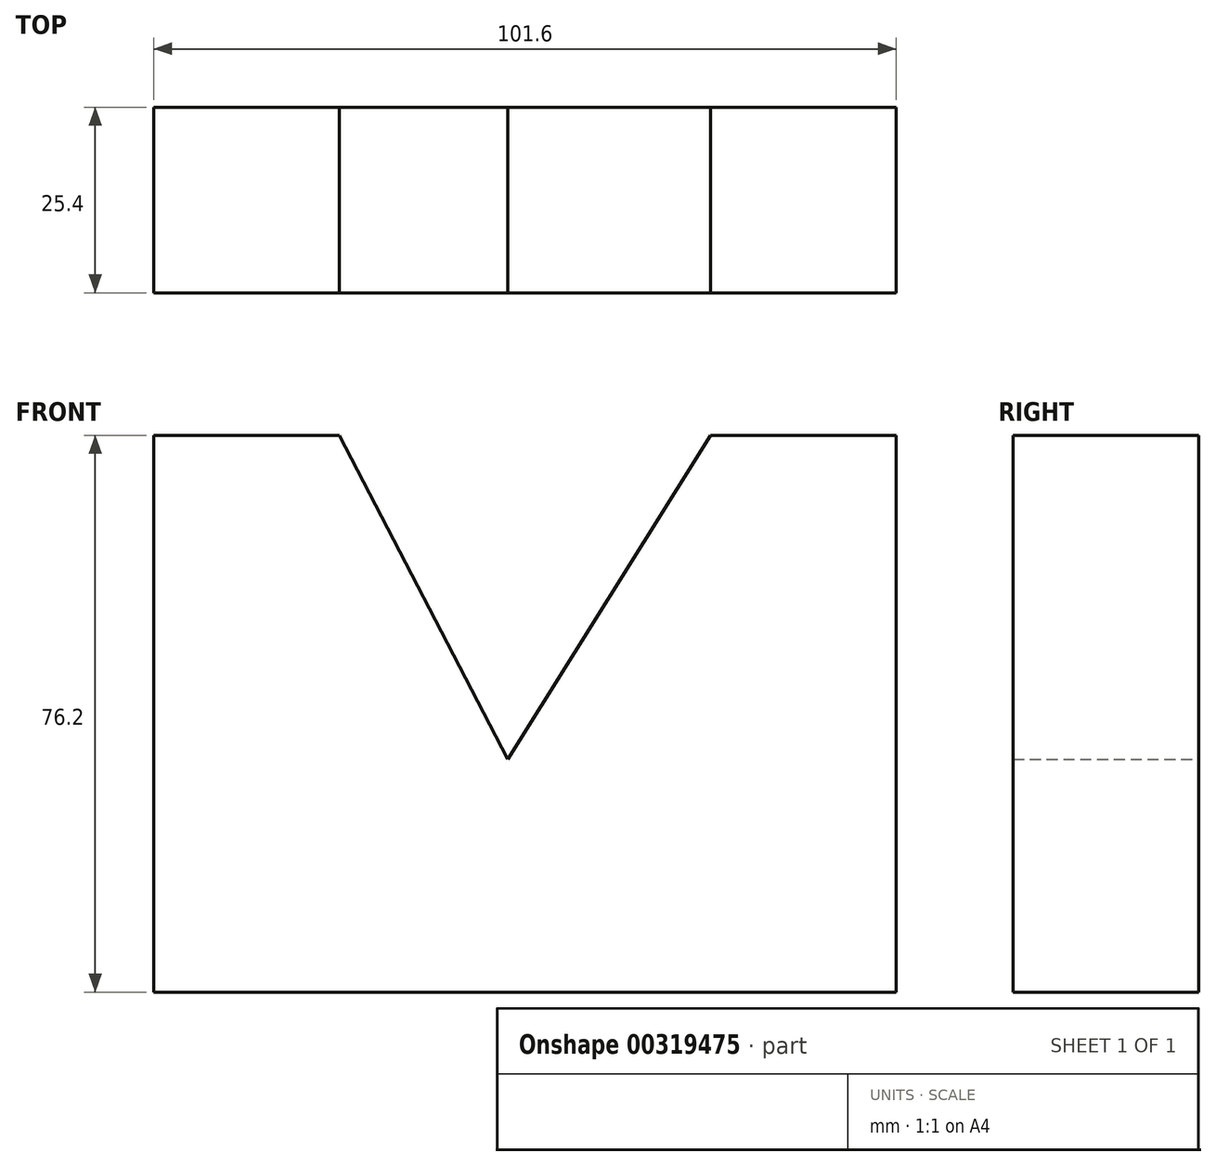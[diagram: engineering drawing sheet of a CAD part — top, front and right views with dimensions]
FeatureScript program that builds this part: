
annotation { "Feature Type Name" : "Feature", "Feature Type Description" : "" }
export const myFeature = defineFeature(function(context is Context, id is Id, definition is map)
    precondition{}
    {
        {
            var Q0;
            Q0=qCreatedBy(makeId("Front.planeOp"),FACE);
            var sketch = newSketch(context, id + "F0", { "sketchPlane" : qUnion([Q0])});
            skLineSegment(sketch, "E0", {"start": v(-43.24, -66.74) * mm, "end": v(58.36, -66.74) * mm});
            skLineSegment(sketch, "E1", {"start": v(58.36, 9.46) * mm, "end": v(58.36, -66.74) * mm});
            skLineSegment(sketch, "E2", {"start": v(-43.24, -66.74) * mm, "end": v(-43.24, 9.46) * mm});
            skLineSegment(sketch, "E3", {"start": v(-43.24, 9.46) * mm, "end": v(-17.84, 9.46) * mm});
            skLineSegment(sketch, "E4", {"start": v(58.36, 9.46) * mm, "end": v(32.96, 9.46) * mm});
            skLineSegment(sketch, "E5", {"start": v(-17.84, 9.46) * mm, "end": v(5.24, -34.87) * mm});
            skLineSegment(sketch, "E6", {"start": v(32.96, 9.46) * mm, "end": v(5.24, -34.87) * mm});
            skSolve(sketch);
        }
        {
            var Q0;
            Q0=makeQuery(id+"F0.imprint","IMPRINT",FACE,{"disambiguationData":[TD([[makeQuery(id+"F0.imprint","IMPRINT",EDGE,{"derivedFrom":sQuery(id+"F0.wireOp",EDGE,"E0")}),1.0]])]});
            extrude(context, id + "F1", {"entities" : qUnion([Q0]), "depth" : 25.4 * mm});
        }
    });
